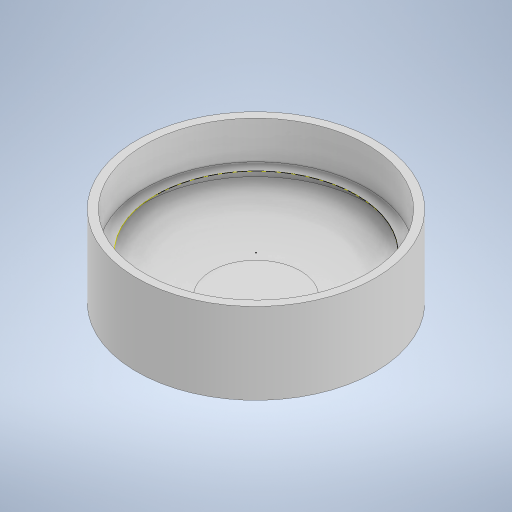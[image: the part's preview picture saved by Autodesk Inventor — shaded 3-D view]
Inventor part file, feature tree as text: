
AUTODESK INVENTOR PART (.ipt)
format: ipt  version: 2023 (Build 270158000, 158)  size: 304,640 bytes
history: native  units: in
note: dims shown in document units (in); Inventor stores cm internally (conversion verified against a paired STEP export)
features: extrude x8, sketch x8, fillet x3, shell x1
ambient origin geometry x8: Origin, YZ Plane, XZ Plane, XY Plane, X Axis, Y Axis, Z Axis, Center Point
bodies: Solid1 (feature_tree)
feature tree (20):
  extrude  "Extrusion1"  Depth=0.249in TaperAngle=0.0deg
  extrude  "Extrusion2"  Depth=0.025in TaperAngle=0.0deg
  fillet  "Fillet1"  Radius=0.1in
  fillet  "Fillet2"  Radius=0.6in
  fillet  "Fillet3"  Radius=0.01in
  shell  "Shell1"  Thickness=0.025in
  sketch  "Sketch3"  dims[d10=1.0in d11=0.0in d12=0.03in d13=0.0in]
  extrude  "Extrusion3"  Depth=0.03in TaperAngle=0.0deg
  extrude  "Extrusion4"  Depth=0.2in TaperAngle=0.0deg
  extrude  "Extrusion6"  Depth=0.2in TaperAngle=0.0deg
  extrude  "Extrusion7"  Depth=0.0344in
  extrude  "Extrusion8"  TaperAngle=0.0deg  [1 undecoded]
  extrude  "Extrusion9"  [1 undecoded]
  sketch  "Sketch11"
  sketch  "Sketch1"  dims[d0=1.26in d1=0.249in d2=0.0in]
  sketch  "Sketch2"  dims[d3=1.05in d4=0.044in d5=0.0in d6=0.1in d7=0.6in d8=0.01in d9=0.025in]
  sketch  "Sketch5"  dims[d16=0.5in d17=0.0in d18=0.2in d19=0.0in]
  sketch  "Sketch7"  dims[d20=0.2in d21=0.0in d22=0.1875in d23=0.0in]
  sketch  "Sketch8"  dims[d24=0.5in d25=0.0344in]
  sketch  "Sketch9"  dims[d26=0.0in d27=0.0in]
note: 2 required parameter values undecoded (feature->parameter linkage not recoverable at this tier; creation-order binding heuristic only, values carry confidence <= 0.55)
